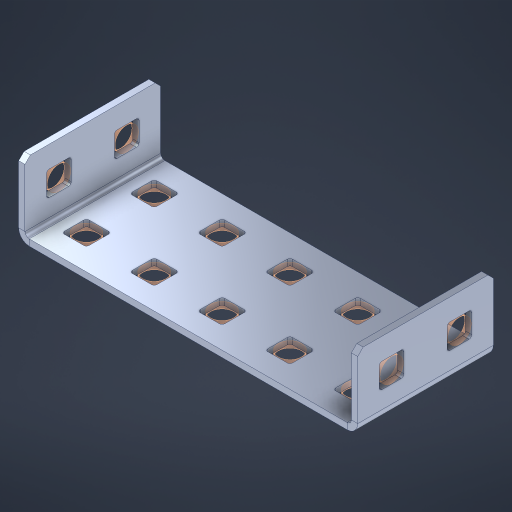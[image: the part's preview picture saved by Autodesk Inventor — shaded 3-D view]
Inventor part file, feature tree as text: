
AUTODESK INVENTOR PART (.ipt)
format: ipt  version: 2023 (Build 270158000, 158)  size: 529,408 bytes
history: native  units: in
note: dims shown in document units (in); Inventor stores cm internally (conversion verified against a paired STEP export)
features: other x55, extrude x13, sheet_metal_op x10, sketch x8, mirror x1, pattern_linear x1, chamfer x1
ambient origin geometry x8: Origin, YZ Plane, XZ Plane, XY Plane, X Axis, Y Axis, Z Axis, Center Point
bodies: Solid1 (feature_tree), Body (feature_tree)
feature tree (89):
  other  "Table"
  other  "Steel C 1x5x1x35"
  other  "Steel C 1x5x1x34"
  other  "Steel C 1x5x1x33"
  other  "Steel C 1x5x1x32"
  other  "Steel C 1x5x1x31"
  other  "Steel C 1x5x1x30"
  other  "Steel C 1x5x1x29"
  other  "Steel C 1x5x1x28"
  other  "Steel C 1x5x1x27"
  other  "Steel C 1x5x1x26"
  other  "Steel C 1x5x1x25"
  other  "Steel C 1x5x1x24"
  other  "Steel C 1x5x1x23"
  other  "Steel C 1x5x1x22"
  other  "Steel C 1x5x1x21"
  other  "Steel C 1x5x1x20"
  other  "Steel C 1x5x1x19"
  other  "Steel C 1x5x1x18"
  other  "Steel C 1x5x1x17"
  other  "Steel C 1x5x1x16"
  other  "Steel C 1x5x1x15"
  other  "Steel C 1x5x1x14"
  other  "Steel C 1x5x1x13"
  other  "Steel C 1x5x1x12"
  other  "Steel C 1x5x1x11"
  other  "Steel C 1x5x1x10"
  other  "Steel C 1x5x1x9"
  other  "Steel C 1x5x1x8"
  other  "Steel C 1x5x1x7"
  other  "Steel C 1x5x1x6"
  other  "Steel C 1x5x1x5"
  other  "Steel C 1x5x1x4"
  other  "Steel C 1x5x1x3"
  other  "Steel C 1x5x1x2"
  other  "Steel C 1x5x1x1"
  other  "Flange Pattern Plane"
  sheet_metal_op  "Flange Pattern"
  sheet_metal_op  "Body Pattern"
  other  "Arc Length"
  mirror  "Notch Mirror"
  pattern_linear  "Notch Pattern"  Spacing1=0.1875in  [1 undecoded]
  chamfer  "End Chamfer"
  extrude  "Half Cut"  Depth=0.0469in
  sketch  "Sketch1"  dims[d0=2.5in]
  other  "Plate1"
  sketch  "Sketch2"  dims[d1=1.0in]
  other  "Plate2"
  sheet_metal_op  "Bend1"
  sheet_metal_op  "Corner1"
  sketch  "Sketch3"  dims[d2=0.0469in]
  other  "Flange Pattern Sketch"
  sketch  "Sketch7"  dims[d3=0.0469in]
  other  "Srf1"
  other  "Srf2"
  sketch  "Sketch8"  dims[d4=0.0234in]
  sketch  "Sketch9"  dims[d5=0.0938in]
  other  "Srf91"
  sheet_metal_op  "Body Pattern Sketch"
  other  "Srf92"
  sketch  "Sketch13"  dims[d6=0.0469in]
  sketch  "Sketch14"  dims[d7=0.5in d8=90.0deg d9=0.0312in d10=0.1875in d11=0.0469in d12=0.0469in d16=0.182in d17=0.02in d18=0.0469in d19=0.0in d20=0.25in d21=0.25in d46=0.172in d47=1.0in d48=0.0in d49=0.182in d50=0.02in d51=0.25in d52=0.25in d53=0.0469in d54=0.0in d55=0.172in d56=1.0in d57=0.0in d60=0.7874in d62=0.5in d63=1.9685in d65=0.5in d85=0.1227in d86=0.1659in d88=0.04in d89=0.0469in d90=0.0in d91=0.04in d92=0.0491in d95=2.5in d96=0.04in d97=0.25in d98=45.0deg d101=0.0in d102=2.497in d131=2.5in d132=0.7874in d134=0.5in d139=0.5in]
  other  "Srf856"
  other  "Srf1310"
  other  "Srf1311"
  other  "Srf1376"
  other  "Srf1377"
  other  "Srf1755"
  other  "Srf1942"
  other  "Srf1943"
  other  "Srf1944"
  other  "Srf1945"
  sheet_metal_op  "Flange Stamp"
  sheet_metal_op  "Flange Circle"
  sheet_metal_op  "Body Stamp"
  sheet_metal_op  "Body Circle"
  sheet_metal_op  "Notch"
  extrude  "ExtrusionSrf2"  Depth=0.0469in
  extrude  "ExtrusionSrf92"  Depth=0.182in
  extrude  "ExtrusionSrf856"  Depth=0.02in
  extrude  "ExtrusionSrf1310"  Depth=0.0469in
  extrude  "ExtrusionSrf1311"  TaperAngle=0.0deg  [1 undecoded]
  extrude  "ExtrusionSrf1376"  Depth=0.25in
  extrude  "ExtrusionSrf1377"  Depth=0.25in
  extrude  "ExtrusionSrf1755"  Depth=0.5in
  extrude  "ExtrusionSrf1942"  Depth=1.0in TaperAngle=0.0deg
  extrude  "ExtrusionSrf1943"  Depth=0.182in
  extrude  "ExtrusionSrf1944"  Depth=0.02in
  extrude  "ExtrusionSrf1945"  Depth=0.25in
note: 2 required parameter values undecoded (feature->parameter linkage not recoverable at this tier; creation-order binding heuristic only, values carry confidence <= 0.55)
